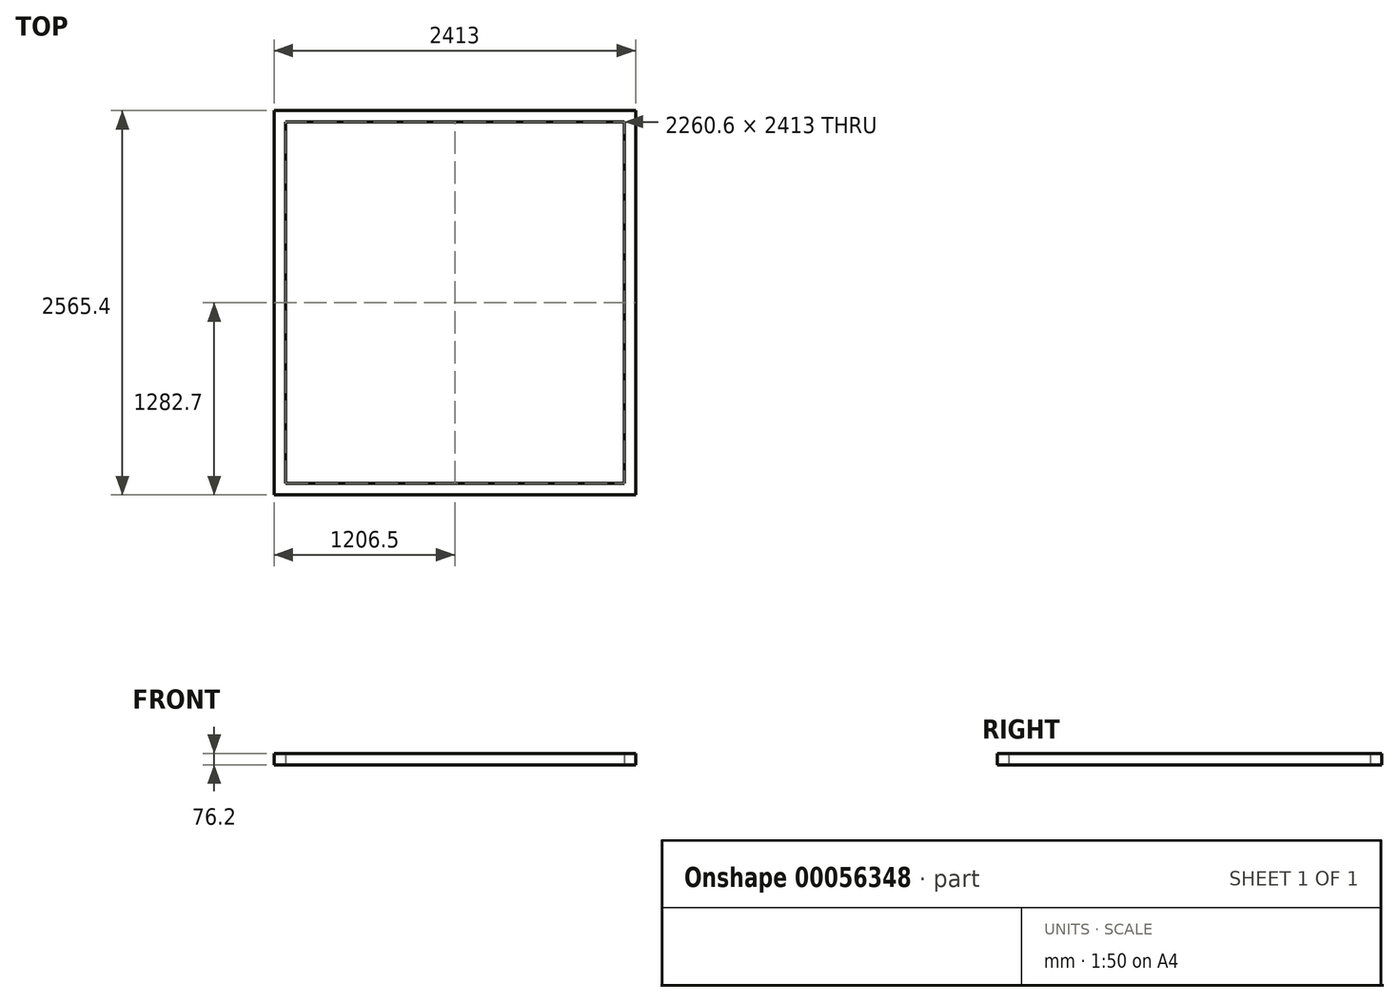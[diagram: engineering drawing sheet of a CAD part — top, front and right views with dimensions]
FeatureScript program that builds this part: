
annotation { "Feature Type Name" : "Feature", "Feature Type Description" : "" }
export const myFeature = defineFeature(function(context is Context, id is Id, definition is map)
    precondition{}
    {
        {
            var Q0;
            Q0=qCreatedBy(makeId("Top.planeOp"),FACE);
            var sketch = newSketch(context, id + "F0", { "sketchPlane" : qUnion([Q0])});
            skLineSegment(sketch, "E0.bottom", {"start": v(-1265.54, -109.93) * mm, "end": v(1147.46, -109.93) * mm});
            skLineSegment(sketch, "E0.top", {"start": v(-1265.54, -186.13) * mm, "end": v(1147.46, -186.13) * mm});
            skLineSegment(sketch, "E0.left", {"start": v(-1265.54, -109.93) * mm, "end": v(-1265.54, -186.13) * mm});
            skLineSegment(sketch, "E0.right", {"start": v(1147.46, -109.93) * mm, "end": v(1147.46, -186.13) * mm});
            skSolve(sketch);
        }
        {
            var Q0;
            Q0=makeQuery(id+"F0.imprint","IMPRINT",FACE,{"disambiguationData":[TD([[makeQuery(id+"F0.imprint","IMPRINT",EDGE,{"derivedFrom":sQuery(id+"F0.wireOp",EDGE,"E0.bottom")}),-1.0]])]});
            extrude(context, id + "F1", {"entities" : qUnion([Q0]), "depth" : 76.2 * mm});
        }
        {
            var Q0;
            Q0=makeQuery(id+"F1.opExtrude","SWEPT_FACE",FACE,{"disambiguationData":[OSD([sQuery(id+"F0.wireOp",EDGE,"E0.top")])]});
            var sketch = newSketch(context, id + "F2", { "sketchPlane" : qUnion([Q0])});
            skLineSegment(sketch, "E1", {"start": v(-1265.54, 76.2) * mm, "end": v(-1189.34, 76.2) * mm});
            skLineSegment(sketch, "E2", {"start": v(-1189.34, 76.2) * mm, "end": v(-1189.34, 0) * mm});
            skLineSegment(sketch, "E3", {"start": v(1147.46, 76.2) * mm, "end": v(1071.26, 76.2) * mm});
            skLineSegment(sketch, "E4", {"start": v(1071.26, 76.2) * mm, "end": v(1071.26, 0) * mm});
            skSolve(sketch);
        }
        {
            var Q0;
            Q0=makeQuery(id+"F2.imprint","IMPRINT",FACE,{"disambiguationData":[TD([[makeQuery(id+"F2.imprint","IMPRINT",EDGE,{"derivedFrom":sQuery(id+"F2.wireOp",EDGE,"E1")}),-1.0]])]});
            var Q1;
            Q1=makeQuery(id+"F2.imprint","IMPRINT",FACE,{"disambiguationData":[TD([[makeQuery(id+"F2.imprint","IMPRINT",EDGE,{"derivedFrom":sQuery(id+"F2.wireOp",EDGE,"E3")}),-1.0]])]});
            extrude(context, id + "F3", {"entities" : qUnion([Q0, Q1]), "operationType" : NewBodyOperationType.ADD, "depth" : 2489.2 * mm});
        }
        {
            var Q0;
            Q0=makeQuery(id+"F3.opExtrude","SWEPT_FACE",FACE,{"disambiguationData":[OSD([sQuery(id+"F2.wireOp",EDGE,"E2")])]});
            var sketch = newSketch(context, id + "F4", { "sketchPlane" : qUnion([Q0])});
            skLineSegment(sketch, "E5", {"start": v(-2675.33, 76.2) * mm, "end": v(-2599.13, 76.2) * mm});
            skLineSegment(sketch, "E6", {"start": v(-2599.13, 76.2) * mm, "end": v(-2599.13, 0) * mm});
            skSolve(sketch);
        }
        {
            var Q0;
            Q0=makeQuery(id+"F3.opExtrude","CAP_FACE",FACE,{"disambiguationData":[OSD([sQuery(id+"F0.wireOp",EDGE,"E0.top"),sQuery(id+"F0.wireOp",EDGE,"E0.left"),sQuery(id+"F2.wireOp",EDGE,"E1"),sQuery(id+"F2.wireOp",EDGE,"E2")])],"isStart":false});
            var sketch = newSketch(context, id + "F5", { "sketchPlane" : qUnion([Q0])});
            skSolve(sketch);
        }
        {
            var Q0;
            Q0 = qSketchRegion(id + "F5", true);
            var Q1;
            Q1=makeQuery(id+"F4.imprint","IMPRINT",FACE,{"disambiguationData":[TD([[makeQuery(id+"F4.imprint","IMPRINT",EDGE,{"derivedFrom":sQuery(id+"F4.wireOp",EDGE,"E5")}),-1.0]])]});
            extrude(context, id + "F6", {"entities" : qUnion([Q0, Q1]), "operationType" : NewBodyOperationType.ADD, "depth" : 2336.8 * mm});
        }
    });
